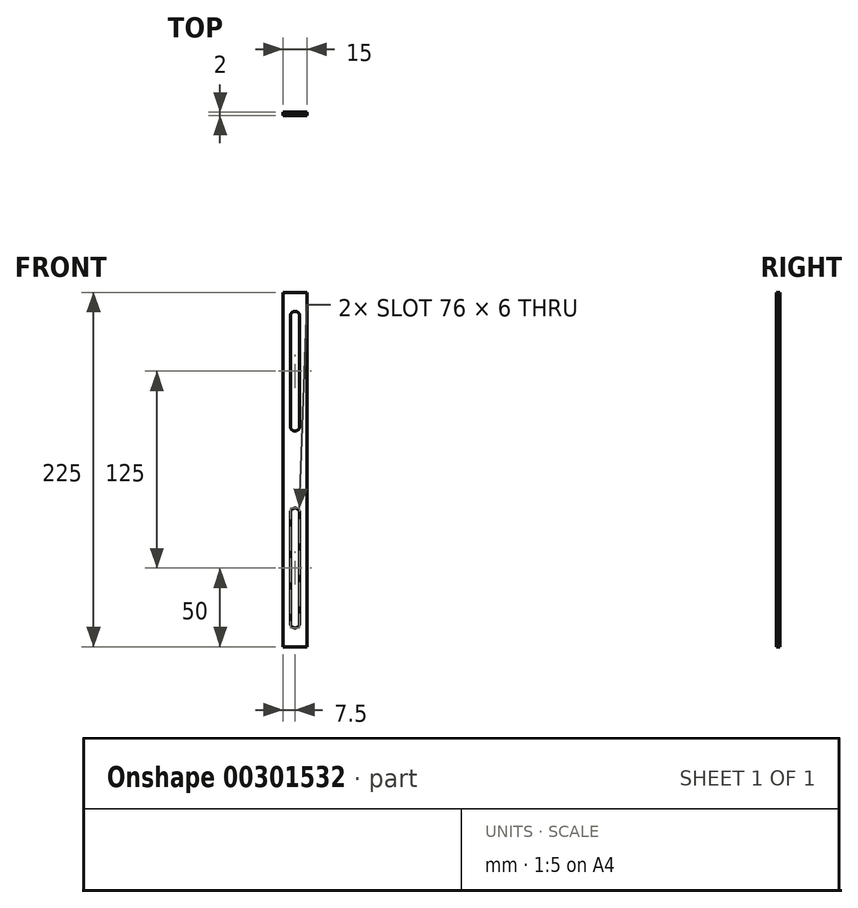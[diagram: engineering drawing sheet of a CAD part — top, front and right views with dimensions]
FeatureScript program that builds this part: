
annotation { "Feature Type Name" : "Feature", "Feature Type Description" : "" }
export const myFeature = defineFeature(function(context is Context, id is Id, definition is map)
    precondition{}
    {
        {
            var Q0;
            Q0=qCreatedBy(makeId("Front.planeOp"),FACE);
            var sketch = newSketch(context, id + "F0", { "sketchPlane" : qUnion([Q0])});
            skLineSegment(sketch, "E0.bottom", {"start": v(0, 0) * mm, "end": v(15, 0) * mm});
            skLineSegment(sketch, "E0.top", {"start": v(0, 225) * mm, "end": v(15, 225) * mm});
            skLineSegment(sketch, "E0.left", {"start": v(0, 0) * mm, "end": v(0, 225) * mm});
            skLineSegment(sketch, "E0.right", {"start": v(15, 0) * mm, "end": v(15, 225) * mm});
            skCircle(sketch, "E1", {"center": v(7.5, 210) * mm, "radius": 3 * mm});
            skPoint(sketch, "E2", {"position": v(7.5, 225) * mm});
            skCircle(sketch, "E3.0.1.0", {"center": v(7.5, 140) * mm, "radius": 3 * mm});
            skLineSegment(sketch, "E3.direction1", {"start": v(7.5, 210) * mm, "end": v(32.5, 210) * mm, "construction": true});
            skLineSegment(sketch, "E3.direction2", {"start": v(7.5, 210) * mm, "end": v(7.5, 140) * mm, "construction": true});
            skLineSegment(sketch, "E4", {"start": v(4.5, 85) * mm, "end": v(4.5, 15) * mm});
            skLineSegment(sketch, "E5", {"start": v(10.5, 85) * mm, "end": v(10.5, 15) * mm});
            skArc(sketch, "E6", {"start": v(4.5, 15) * mm, "mid": v(7.5, 12) * mm, "end": v(10.5, 15) * mm});
            skArc(sketch, "E7", {"start": v(10.5, 85) * mm, "mid": v(7.5, 88) * mm, "end": v(4.5, 85) * mm});
            skLineSegment(sketch, "E8", {"start": v(4.5, 210) * mm, "end": v(4.5, 140) * mm});
            skLineSegment(sketch, "E9", {"start": v(10.5, 210) * mm, "end": v(10.5, 140) * mm});
            skSolve(sketch);
        }
        {
            var Q0;
            Q0=qSketchRegion(id+"F0",true);
            extrude(context, id + "F1", {"entities" : qUnion([Q0]), "depth" : 2 * mm});
        }
    });
